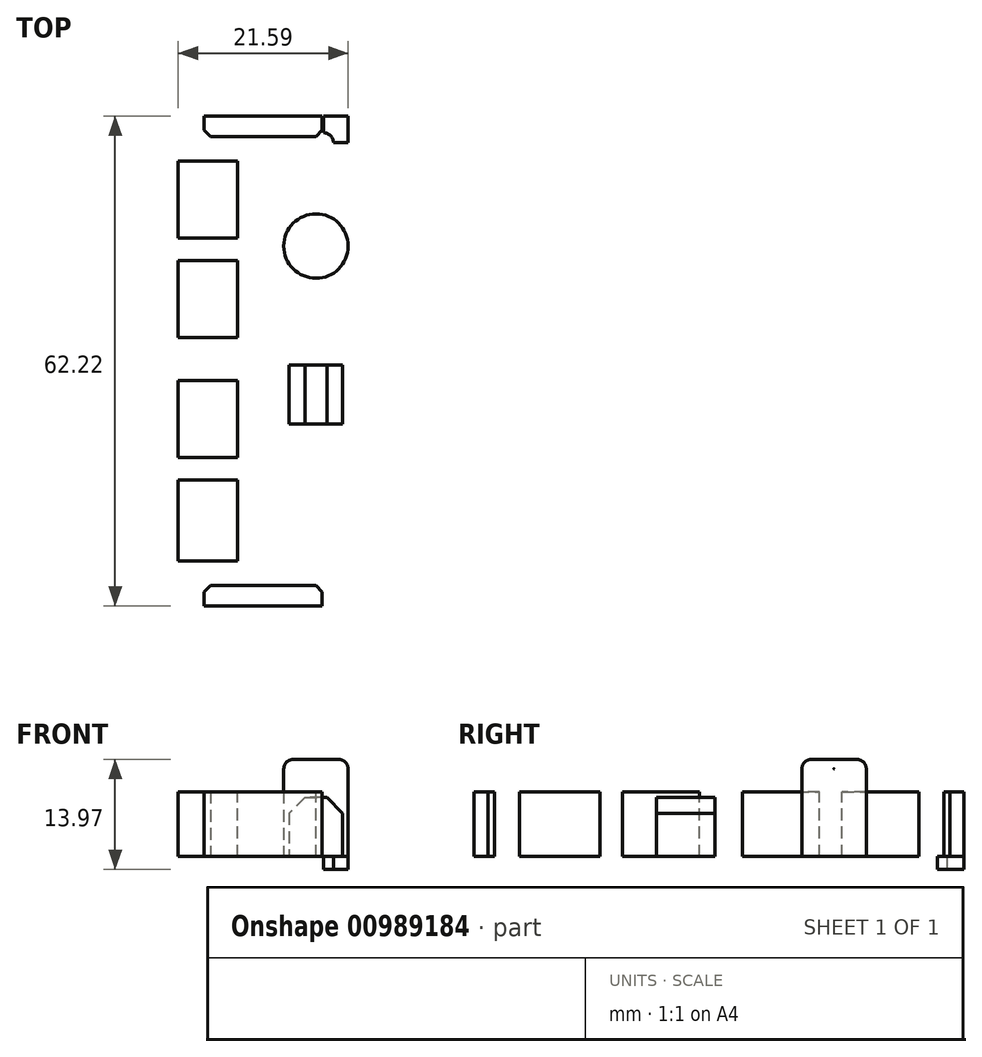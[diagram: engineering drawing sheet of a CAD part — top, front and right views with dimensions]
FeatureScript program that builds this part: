
annotation { "Feature Type Name" : "Feature", "Feature Type Description" : "" }
export const myFeature = defineFeature(function(context is Context, id is Id, definition is map)
    precondition{}
    {
        {
            var Q0;
            Q0=qCreatedBy(makeId("Top.planeOp"),FACE);
            var sketch = newSketch(context, id + "F0", { "sketchPlane" : qUnion([Q0])});
            skLineSegment(sketch, "E0.bottom", {"start": v(-10.8, -31.1) * mm, "end": v(10.8, -31.1) * mm});
            skLineSegment(sketch, "E0.top", {"start": v(-10.8, 31.1) * mm, "end": v(10.8, 31.1) * mm});
            skLineSegment(sketch, "E0.left", {"start": v(-10.8, -31.1) * mm, "end": v(-10.8, 31.1) * mm});
            skLineSegment(sketch, "E0.right", {"start": v(10.8, -31.1) * mm, "end": v(10.8, 31.1) * mm});
            skPoint(sketch, "E0.middle", {"position": v(0, 0) * mm});
            skSolve(sketch);
        }
        {
            var Q0;
            Q0 = qSketchRegion(id + "F0", true);
            extrude(context, id + "F1", {"entities" : qUnion([Q0]), "depth" : 1.63 * mm, "offsetDistance" : 25 * mm});
        }
        {
            var Q0;
            Q0=makeQuery(id+"F1.opExtrude","CAP_FACE",FACE,{"disambiguationData":[OSD([sQuery(id+"F0.wireOp",EDGE,"E0.bottom"),sQuery(id+"F0.wireOp",EDGE,"E0.top"),sQuery(id+"F0.wireOp",EDGE,"E0.left"),sQuery(id+"F0.wireOp",EDGE,"E0.right")])],"isStart":false});
            var sketch = newSketch(context, id + "F2", { "sketchPlane" : qUnion([Q0])});
            skCircle(sketch, "E1", {"center": v(7.67, 27.75) * mm, "radius": 1.25 * mm});
            skLineSegment(sketch, "E2.bottom", {"start": v(10.8, 31.1) * mm, "end": v(7.67, 31.1) * mm});
            skLineSegment(sketch, "E2.top", {"start": v(10.8, 27.75) * mm, "end": v(7.67, 27.75) * mm});
            skLineSegment(sketch, "E2.left", {"start": v(10.8, 31.1) * mm, "end": v(10.8, 27.75) * mm});
            skLineSegment(sketch, "E2.right", {"start": v(7.67, 31.1) * mm, "end": v(7.67, 27.75) * mm});
            skCircle(sketch, "E3.MirrorC", {"center": v(-7.67, 27.75) * mm, "radius": 1.25 * mm});
            skCircle(sketch, "E4.MirrorC", {"center": v(-7.67, -27.75) * mm, "radius": 1.25 * mm});
            skCircle(sketch, "E5.MirrorC", {"center": v(7.67, -27.75) * mm, "radius": 1.25 * mm});
            skSolve(sketch);
        }
        {
            var Q0;
            Q0=makeQuery(id+"F1.opExtrude","CAP_FACE",FACE,{"disambiguationData":[OSD([sQuery(id+"F0.wireOp",EDGE,"E0.bottom"),sQuery(id+"F0.wireOp",EDGE,"E0.top"),sQuery(id+"F0.wireOp",EDGE,"E0.left"),sQuery(id+"F0.wireOp",EDGE,"E0.right")])],"isStart":false});
            var sketch = newSketch(context, id + "F3", { "sketchPlane" : qUnion([Q0])});
            skLineSegment(sketch, "E6", {"start": v(6.7, 31.1) * mm, "end": v(6.7, 14.6) * mm});
            skCircle(sketch, "E7", {"center": v(6.7, 14.6) * mm, "radius": 4.1 * mm});
            skLineSegment(sketch, "E8", {"start": v(6.7, 10.52) * mm, "end": v(6.7, -0.52) * mm});
            skPoint(sketch, "E9.middle", {"position": v(6.7, -7.07) * mm});
            skPoint(sketch, "E10.middle", {"position": v(20.4, -12.22) * mm});
            skLineSegment(sketch, "E11", {"start": v(6.7, -0.52) * mm, "end": v(3.32, -0.52) * mm});
            skLineSegment(sketch, "E12.MirrorCS", {"start": v(6.7, -0.52) * mm, "end": v(10.1, -0.52) * mm});
            skLineSegment(sketch, "E13", {"start": v(3.32, -0.52) * mm, "end": v(3.32, -7.97) * mm});
            skLineSegment(sketch, "E14", {"start": v(10.1, -0.52) * mm, "end": v(10.1, -7.97) * mm});
            skLineSegment(sketch, "E15", {"start": v(10.1, -7.97) * mm, "end": v(3.32, -7.97) * mm});
            skSolve(sketch);
        }
        {
            var Q0;
            {var subQ0=sQuery(id+"F3.wireOp",EDGE,"E7");var subQ5=makeQuery(id+"F3.imprint","IMPRINT",VERTEX,{"derivedFrom":subQ0});Q0=makeQuery(id+"F3.imprint","IMPRINT",FACE,{"disambiguationData":[TD([[makeQuery(id+"F3.imprint","IMPRINT",EDGE,{"disambiguationData":[TD([[subQ5,1.0]])],"derivedFrom":subQ0}),1.0]])]});}
            extrude(context, id + "F4", {"entities" : qUnion([Q0]), "operationType" : NewBodyOperationType.ADD, "depth" : 12.34 * mm, "offsetDistance" : 25 * mm});
        }
        {
            var Q0;
            Q0=makeQuery(id+"F3.imprint","IMPRINT",FACE,{"disambiguationData":[TD([[makeQuery(id+"F3.imprint","IMPRINT",EDGE,{"derivedFrom":sQuery(id+"F3.wireOp",EDGE,"E11")}),1.0]])]});
            extrude(context, id + "F5", {"entities" : qUnion([Q0]), "operationType" : NewBodyOperationType.ADD, "depth" : 7.5 * mm, "offsetDistance" : 25 * mm});
        }
        {
            var Q0;
            {var subQ0=sQuery(id+"F2.wireOp",EDGE,"E2.top");var subQ1=sQuery(id+"F2.wireOp",EDGE,"E1");var subQ2=makeQuery(id+"F2.imprint","INTERSECT",VERTEX,{"derivedFrom":[subQ1,subQ0]});Q0=makeQuery(id+"F2.imprint","IMPRINT",FACE,{"disambiguationData":[TD([[makeQuery(id+"F2.imprint","IMPRINT",EDGE,{"disambiguationData":[TD([[subQ2,1.0]])],"derivedFrom":subQ1}),1.0]])]});}
            var Q1;
            {var subQ0=sQuery(id+"F2.wireOp",EDGE,"E2.top");var subQ1=sQuery(id+"F2.wireOp",EDGE,"E1");var subQ2=makeQuery(id+"F2.imprint","INTERSECT",VERTEX,{"derivedFrom":[subQ1,subQ0]});Q1=makeQuery(id+"F2.imprint","IMPRINT",FACE,{"disambiguationData":[TD([[makeQuery(id+"F2.imprint","IMPRINT",EDGE,{"disambiguationData":[TD([[subQ2,-1.0]])],"derivedFrom":subQ1}),1.0]])]});}
            var Q2;
            Q2=makeQuery(id+"F2.imprint","IMPRINT",FACE,{"disambiguationData":[TD([[makeQuery(id+"F2.imprint","IMPRINT",EDGE,{"derivedFrom":sQuery(id+"F2.wireOp",EDGE,"E3.MirrorC")}),-1.0]])]});
            var Q3;
            Q3=makeQuery(id+"F2.imprint","IMPRINT",FACE,{"disambiguationData":[TD([[makeQuery(id+"F2.imprint","IMPRINT",EDGE,{"derivedFrom":sQuery(id+"F2.wireOp",EDGE,"E4.MirrorC")}),1.0]])]});
            var Q4;
            Q4=makeQuery(id+"F2.imprint","IMPRINT",FACE,{"disambiguationData":[TD([[makeQuery(id+"F2.imprint","IMPRINT",EDGE,{"derivedFrom":sQuery(id+"F2.wireOp",EDGE,"E5.MirrorC")}),-1.0]])]});
            extrude(context, id + "F6", {"entities" : qUnion([Q0, Q1, Q2, Q3, Q4]), "operationType" : NewBodyOperationType.REMOVE, "oppositeDirection" : true, "depth" : 25 * mm, "offsetDistance" : 25 * mm});
        }
        {
            var Q0;
            Q0=makeQuery(id+"F5.opExtrude","CAP_EDGE",EDGE,{"disambiguationData":[OSD([sQuery(id+"F3.wireOp",EDGE,"E13")])],"isStart":false});
            var Q1;
            Q1=makeQuery(id+"F5.opExtrude","CAP_EDGE",EDGE,{"disambiguationData":[OSD([sQuery(id+"F3.wireOp",EDGE,"E14")])],"isStart":false});
            chamfer(context, id + "F7", {"entities" : qUnion([Q0, Q1]), "width" : 2 * mm, "tangentPropagation" : true});
        }
        {
            var Q0;
            {var subQ0=sQuery(id+"F3.wireOp",EDGE,"E7");var subQ1=makeQuery(id+"F3.imprint","IMPRINT",VERTEX,{"derivedFrom":subQ0});var subQ3=makeQuery(id+"F3.imprint","INTERSECT",VERTEX,{"derivedFrom":[sQuery(id+"F3.wireOp",EDGE,"E6"),subQ0]});Q0=makeQuery(id+"F4.opExtrude","CAP_EDGE",EDGE,{"disambiguationData":[OSD([subQ0]),TDD([makeQuery(id+"F3.imprint","IMPRINT",EDGE,{"disambiguationData":[TD([[subQ3,1.0]])],"derivedFrom":subQ0}),makeQuery(id+"F3.imprint","IMPRINT",EDGE,{"disambiguationData":[TD([[subQ1,1.0]])],"derivedFrom":subQ0}),makeQuery(id+"F3.imprint","IMPRINT",EDGE,{"disambiguationData":[TD([[subQ1,-1.0]])],"derivedFrom":subQ0})])],"isStart":false});}
            fillet(context, id + "F8", {"entities" : qUnion([Q0]), "radius" : 1.2 * mm, "tangentPropagation" : true, "allowEdgeOverflow" : false});
        }
        {
            var Q0;
            Q0=makeQuery(id+"F1.opExtrude","CAP_FACE",FACE,{"disambiguationData":[OSD([sQuery(id+"F0.wireOp",EDGE,"E0.bottom"),sQuery(id+"F0.wireOp",EDGE,"E0.top"),sQuery(id+"F0.wireOp",EDGE,"E0.left"),sQuery(id+"F0.wireOp",EDGE,"E0.right")])],"isStart":false});
            var sketch = newSketch(context, id + "F9", { "sketchPlane" : qUnion([Q0])});
            skPoint(sketch, "E16.middle", {"position": v(-9.76, 0) * mm});
            skLineSegment(sketch, "E17", {"start": v(-10.8, 0) * mm, "end": v(-10.8, 25.38) * mm});
            skLineSegment(sketch, "E18.MirrorCS", {"start": v(-10.8, 0) * mm, "end": v(-10.8, -25.38) * mm});
            skLineSegment(sketch, "E19", {"start": v(-10.8, 25.38) * mm, "end": v(-3.29, 25.38) * mm});
            skLineSegment(sketch, "E20.MirrorCS", {"start": v(-10.8, -25.38) * mm, "end": v(-3.29, -25.38) * mm});
            skLineSegment(sketch, "E21", {"start": v(-3.29, 25.38) * mm, "end": v(-3.29, -25.38) * mm});
            skSolve(sketch);
        }
        {
            var Q0;
            Q0=makeQuery(id+"F9.imprint","IMPRINT",FACE,{"disambiguationData":[TD([[makeQuery(id+"F9.imprint","IMPRINT",EDGE,{"derivedFrom":sQuery(id+"F9.wireOp",EDGE,"E17")}),-1.0]])]});
            extrude(context, id + "F10", {"entities" : qUnion([Q0]), "operationType" : NewBodyOperationType.ADD, "depth" : 8.23 * mm, "offsetDistance" : 25 * mm});
        }
        {
            var Q0;
            Q0=makeQuery(id+"F1.opExtrude","CAP_FACE",FACE,{"disambiguationData":[OSD([sQuery(id+"F0.wireOp",EDGE,"E0.bottom"),sQuery(id+"F0.wireOp",EDGE,"E0.top"),sQuery(id+"F0.wireOp",EDGE,"E0.left"),sQuery(id+"F0.wireOp",EDGE,"E0.right")])],"isStart":false});
            var sketch = newSketch(context, id + "F11", { "sketchPlane" : qUnion([Q0])});
            skLineSegment(sketch, "E22", {"start": v(0, 31.1) * mm, "end": v(-7.49, 31.1) * mm});
            skLineSegment(sketch, "E23", {"start": v(-7.49, 31.1) * mm, "end": v(-7.49, 28.53) * mm});
            skLineSegment(sketch, "E24.MirrorCS", {"start": v(7.49, 31.1) * mm, "end": v(7.49, 28.53) * mm});
            skLineSegment(sketch, "E25.MirrorCS", {"start": v(0, 31.1) * mm, "end": v(7.49, 31.1) * mm});
            skLineSegment(sketch, "E26", {"start": v(-7.49, 28.53) * mm, "end": v(7.49, 28.53) * mm});
            skLineSegment(sketch, "E27.MirrorCS", {"start": v(-7.49, -28.53) * mm, "end": v(7.49, -28.53) * mm});
            skLineSegment(sketch, "E28.MirrorCS", {"start": v(0, -31.1) * mm, "end": v(-7.49, -31.1) * mm});
            skLineSegment(sketch, "E29.MirrorCS", {"start": v(0, -31.1) * mm, "end": v(7.49, -31.1) * mm});
            skLineSegment(sketch, "E30.MirrorCS", {"start": v(7.49, -31.1) * mm, "end": v(7.49, -28.53) * mm});
            skLineSegment(sketch, "E31.MirrorCS", {"start": v(-7.49, -31.1) * mm, "end": v(-7.49, -28.53) * mm});
            skSolve(sketch);
        }
        {
            var Q0;
            {var subQ6=sQuery(id+"F11.wireOp",EDGE,"E22");Q0=makeQuery(id+"F11.imprint","IMPRINT",FACE,{"disambiguationData":[TD([[makeQuery(id+"F11.imprint","IMPRINT",EDGE,{"derivedFrom":subQ6}),-1.0]])]});}
            var Q1;
            {var subQ0=sQuery(id+"F11.wireOp",EDGE,"E26");var subQ1=sQuery(id+"F11.wireOp",EDGE,"E24.MirrorCS");var subQ2=makeQuery(id+"F11.imprint","INTERSECT",VERTEX,{"derivedFrom":[subQ1,subQ0]});Q1=makeQuery(id+"F11.imprint","IMPRINT",FACE,{"disambiguationData":[TD([[makeQuery(id+"F11.imprint","IMPRINT",EDGE,{"disambiguationData":[TD([[subQ2,1.0]])],"derivedFrom":subQ1}),-1.0]])]});}
            var Q2;
            {var subQ0=sQuery(id+"F11.wireOp",EDGE,"E26");var subQ1=sQuery(id+"F11.wireOp",EDGE,"E23");var subQ2=makeQuery(id+"F11.imprint","INTERSECT",VERTEX,{"derivedFrom":[subQ1,subQ0]});Q2=makeQuery(id+"F11.imprint","IMPRINT",FACE,{"disambiguationData":[TD([[makeQuery(id+"F11.imprint","IMPRINT",EDGE,{"disambiguationData":[TD([[subQ2,1.0]])],"derivedFrom":subQ1}),1.0]])]});}
            var Q3;
            {var subQ5=sQuery(id+"F11.wireOp",EDGE,"E28.MirrorCS");Q3=makeQuery(id+"F11.imprint","IMPRINT",FACE,{"disambiguationData":[TD([[makeQuery(id+"F11.imprint","IMPRINT",EDGE,{"derivedFrom":subQ5}),1.0]])]});}
            var Q4;
            {var subQ0=sQuery(id+"F11.wireOp",EDGE,"E30.MirrorCS");var subQ1=sQuery(id+"F11.wireOp",EDGE,"E27.MirrorCS");var subQ2=makeQuery(id+"F11.imprint","INTERSECT",VERTEX,{"derivedFrom":[subQ1,subQ0]});Q4=makeQuery(id+"F11.imprint","IMPRINT",FACE,{"disambiguationData":[TD([[makeQuery(id+"F11.imprint","IMPRINT",EDGE,{"disambiguationData":[TD([[subQ2,1.0]])],"derivedFrom":subQ1}),-1.0]])]});}
            var Q5;
            {var subQ0=sQuery(id+"F11.wireOp",EDGE,"E31.MirrorCS");var subQ1=sQuery(id+"F11.wireOp",EDGE,"E27.MirrorCS");var subQ2=makeQuery(id+"F11.imprint","INTERSECT",VERTEX,{"derivedFrom":[subQ1,subQ0]});Q5=makeQuery(id+"F11.imprint","IMPRINT",FACE,{"disambiguationData":[TD([[makeQuery(id+"F11.imprint","IMPRINT",EDGE,{"disambiguationData":[TD([[subQ2,-1.0]])],"derivedFrom":subQ1}),-1.0]])]});}
            extrude(context, id + "F12", {"entities" : qUnion([Q0, Q1, Q2, Q3, Q4, Q5]), "operationType" : NewBodyOperationType.ADD, "depth" : 8.23 * mm, "offsetDistance" : 25 * mm});
        }
        {
            var Q0;
            Q0=makeQuery(id+"F12.opExtrude","SWEPT_EDGE",EDGE,{"disambiguationData":[OSD([sQuery(id+"F11.wireOp",EDGE,"E23"),sQuery(id+"F11.wireOp",EDGE,"E26")])]});
            var Q1;
            Q1=makeQuery(id+"F12.opExtrude","SWEPT_EDGE",EDGE,{"disambiguationData":[OSD([sQuery(id+"F11.wireOp",EDGE,"E24.MirrorCS"),sQuery(id+"F11.wireOp",EDGE,"E26")])]});
            var Q2;
            Q2=makeQuery(id+"F12.opExtrude","SWEPT_EDGE",EDGE,{"disambiguationData":[OSD([sQuery(id+"F11.wireOp",EDGE,"E27.MirrorCS"),sQuery(id+"F11.wireOp",EDGE,"E31.MirrorCS")])]});
            var Q3;
            Q3=makeQuery(id+"F12.opExtrude","SWEPT_EDGE",EDGE,{"disambiguationData":[OSD([sQuery(id+"F11.wireOp",EDGE,"E27.MirrorCS"),sQuery(id+"F11.wireOp",EDGE,"E30.MirrorCS")])]});
            chamfer(context, id + "F13", {"entities" : qUnion([Q0, Q1, Q2, Q3]), "width" : 0.8 * mm, "tangentPropagation" : true});
        }
        {
            var Q0;
            Q0=makeQuery(id+"F10.opExtrude","CAP_FACE",FACE,{"disambiguationData":[OSD([sQuery(id+"F9.wireOp",EDGE,"E17"),sQuery(id+"F9.wireOp",EDGE,"E18.MirrorCS"),sQuery(id+"F9.wireOp",EDGE,"E19"),sQuery(id+"F9.wireOp",EDGE,"E20.MirrorCS"),sQuery(id+"F9.wireOp",EDGE,"E21")])],"isStart":false});
            var sketch = newSketch(context, id + "F14", { "sketchPlane" : qUnion([Q0])});
            skLineSegment(sketch, "E32", {"start": v(-10.8, 25.38) * mm, "end": v(-10.8, 15.6) * mm});
            skLineSegment(sketch, "E33.bottom", {"start": v(-10.8, 15.6) * mm, "end": v(-3.29, 15.6) * mm});
            skLineSegment(sketch, "E33.top", {"start": v(-10.8, 12.77) * mm, "end": v(-3.29, 12.77) * mm});
            skLineSegment(sketch, "E33.left", {"start": v(-10.8, 15.6) * mm, "end": v(-10.8, 12.77) * mm});
            skLineSegment(sketch, "E33.right", {"start": v(-3.29, 15.6) * mm, "end": v(-3.29, 12.77) * mm});
            skLineSegment(sketch, "E34", {"start": v(-10.8, 12.77) * mm, "end": v(-10.8, 3) * mm});
            skLineSegment(sketch, "E35.bottom", {"start": v(-10.8, 3) * mm, "end": v(-3.29, 3) * mm});
            skLineSegment(sketch, "E35.top", {"start": v(-10.8, -2.49) * mm, "end": v(-3.29, -2.49) * mm});
            skLineSegment(sketch, "E35.left", {"start": v(-10.8, 3) * mm, "end": v(-10.8, -2.49) * mm});
            skLineSegment(sketch, "E35.right", {"start": v(-3.29, 3) * mm, "end": v(-3.29, -2.49) * mm});
            skLineSegment(sketch, "E36", {"start": v(-10.8, -2.49) * mm, "end": v(-10.8, -12.27) * mm});
            skLineSegment(sketch, "E37.bottom", {"start": v(-10.8, -12.27) * mm, "end": v(-3.29, -12.27) * mm});
            skLineSegment(sketch, "E37.top", {"start": v(-10.8, -15.1) * mm, "end": v(-3.29, -15.1) * mm});
            skLineSegment(sketch, "E37.left", {"start": v(-10.8, -12.27) * mm, "end": v(-10.8, -15.1) * mm});
            skLineSegment(sketch, "E37.right", {"start": v(-3.29, -12.27) * mm, "end": v(-3.29, -15.1) * mm});
            skSolve(sketch);
        }
        {
            var Q0;
            Q0=makeQuery(id+"F14.imprint","IMPRINT",FACE,{"disambiguationData":[TD([[makeQuery(id+"F14.imprint","IMPRINT",EDGE,{"derivedFrom":sQuery(id+"F14.wireOp",EDGE,"E33.bottom")}),-1.0]])]});
            var Q1;
            Q1=makeQuery(id+"F14.imprint","IMPRINT",FACE,{"disambiguationData":[TD([[makeQuery(id+"F14.imprint","IMPRINT",EDGE,{"derivedFrom":sQuery(id+"F14.wireOp",EDGE,"E35.bottom")}),-1.0]])]});
            var Q2;
            Q2=makeQuery(id+"F14.imprint","IMPRINT",FACE,{"disambiguationData":[TD([[makeQuery(id+"F14.imprint","IMPRINT",EDGE,{"derivedFrom":sQuery(id+"F14.wireOp",EDGE,"E37.bottom")}),-1.0]])]});
            extrude(context, id + "F15", {"entities" : qUnion([Q0, Q1, Q2]), "operationType" : NewBodyOperationType.REMOVE, "oppositeDirection" : true, "depth" : 8.23 * mm, "offsetDistance" : 25 * mm});
        }
    });
